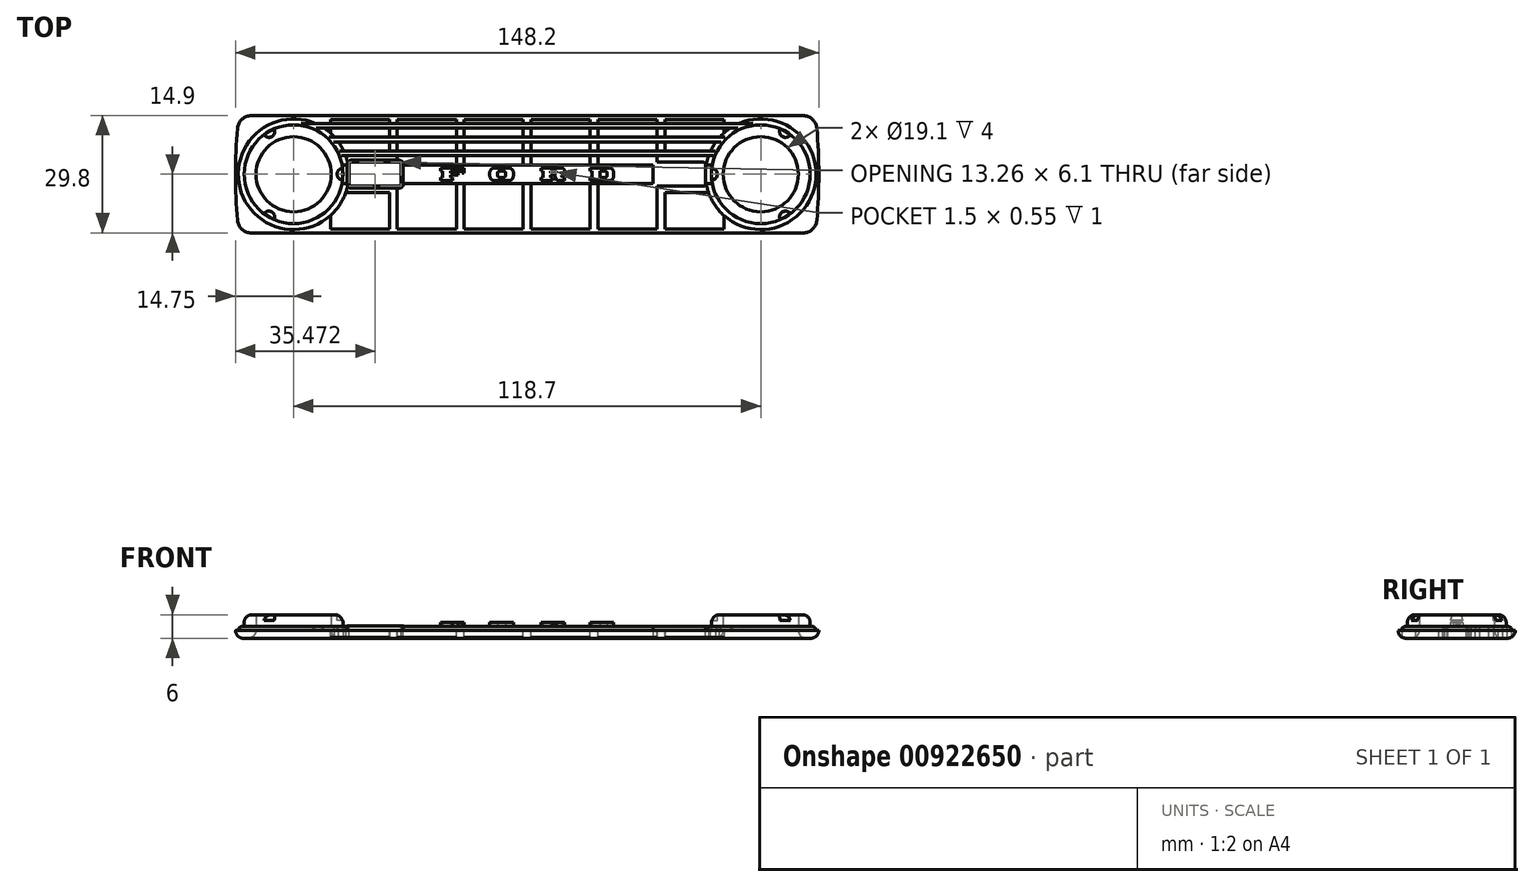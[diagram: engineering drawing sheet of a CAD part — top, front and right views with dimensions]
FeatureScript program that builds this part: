
annotation { "Feature Type Name" : "Feature", "Feature Type Description" : "" }
export const myFeature = defineFeature(function(context is Context, id is Id, definition is map)
    precondition{}
    {
        {
            var Q0;
            Q0=qCreatedBy(makeId("Top.planeOp"),FACE);
            var sketch = newSketch(context, id + "F0", { "sketchPlane" : qUnion([Q0])});
            skLineSegment(sketch, "E0.bottom", {"start": v(73.25, 14.9) * mm, "end": v(-73.25, 14.9) * mm});
            skLineSegment(sketch, "E0.top", {"start": v(73.25, -14.9) * mm, "end": v(-73.25, -14.9) * mm});
            skLineSegment(sketch, "E0.left", {"start": v(73.25, 14.9) * mm, "end": v(73.25, -14.9) * mm, "construction": true});
            skLineSegment(sketch, "E0.right", {"start": v(-73.25, 14.9) * mm, "end": v(-73.25, -14.9) * mm, "construction": true});
            skPoint(sketch, "E0.middle", {"position": v(0, 0) * mm});
            skLineSegment(sketch, "E1.0", {"start": v(-74.1, 15.75) * mm, "end": v(-74.1, -15.75) * mm, "construction": true});
            skLineSegment(sketch, "E1.2", {"start": v(74.1, 15.75) * mm, "end": v(74.1, -15.75) * mm, "construction": true});
            skPoint(sketch, "E2", {"position": v(-74.1, 0) * mm});
            skArc(sketch, "E3", {"start": v(-73.25, 14.9) * mm, "mid": v(-74.1, 0) * mm, "end": v(-73.25, -14.9) * mm});
            skArc(sketch, "E4.MirrorCS", {"start": v(73.25, 14.9) * mm, "mid": v(74.1, 0) * mm, "end": v(73.25, -14.9) * mm});
            skCircle(sketch, "E5", {"center": v(-59.35, 0) * mm, "radius": 9.55 * mm});
            skCircle(sketch, "E6.MirrorC", {"center": v(59.35, 0) * mm, "radius": 9.55 * mm});
            skSolve(sketch);
        }
        {
            var Q0;
            Q0 = qSketchRegion(id + "F0", true);
            extrude(context, id + "F1", {"entities" : qUnion([Q0]), "depth" : 2 * mm, "offsetDistance" : 25 * mm});
        }
        {
            var Q0;
            Q0=makeQuery(id+"F1.opExtrude","CAP_FACE",FACE,{"disambiguationData":[OSD([sQuery(id+"F0.wireOp",EDGE,"E0.bottom"),sQuery(id+"F0.wireOp",EDGE,"E0.top"),sQuery(id+"F0.wireOp",EDGE,"E3"),sQuery(id+"F0.wireOp",EDGE,"E4.MirrorCS"),sQuery(id+"F0.wireOp",EDGE,"E5"),sQuery(id+"F0.wireOp",EDGE,"E6.MirrorC")])],"isStart":true});
            var sketch = newSketch(context, id + "F2", { "sketchPlane" : qUnion([Q0])});
            skLineSegment(sketch, "E7", {"start": v(0, 14.9) * mm, "end": v(0, -14.9) * mm, "construction": true});
            skLineSegment(sketch, "E8.0", {"start": v(-1, 13.9) * mm, "end": v(-1, -13.9) * mm});
            skLineSegment(sketch, "E9.0", {"start": v(-16, 13.9) * mm, "end": v(-16, -13.9) * mm});
            skLineSegment(sketch, "E10.0", {"start": v(-18, 13.9) * mm, "end": v(-18, -13.9) * mm});
            skLineSegment(sketch, "E11.0", {"start": v(-33, 13.9) * mm, "end": v(-33, -13.9) * mm});
            skLineSegment(sketch, "E12.0", {"start": v(-35, 13.9) * mm, "end": v(-35, -13.9) * mm});
            skLineSegment(sketch, "E13.0", {"start": v(-50, 13.9) * mm, "end": v(-50, 10.49) * mm});
            skLineSegment(sketch, "E14.trimOffspring", {"start": v(-50, -10.49) * mm, "end": v(-50, -13.9) * mm});
            skArc(sketch, "E15.trimOffspring", {"start": v(-50, -10.49) * mm, "mid": v(-45.3, 0) * mm, "end": v(-50, 10.49) * mm});
            skLineSegment(sketch, "E16.trimOffspring", {"start": v(-35, -13.9) * mm, "end": v(-50, -13.9) * mm});
            skLineSegment(sketch, "E17.trimOffspring", {"start": v(-35, 13.9) * mm, "end": v(-50, 13.9) * mm});
            skLineSegment(sketch, "E18.trimOffspring", {"start": v(-18, 13.9) * mm, "end": v(-33, 13.9) * mm});
            skLineSegment(sketch, "E19.trimOffspring", {"start": v(-18, -13.9) * mm, "end": v(-33, -13.9) * mm});
            skLineSegment(sketch, "E20.trimOffspring", {"start": v(-1, -13.9) * mm, "end": v(-16, -13.9) * mm});
            skLineSegment(sketch, "E21.trimOffspring", {"start": v(-1, 13.9) * mm, "end": v(-16, 13.9) * mm});
            skLineSegment(sketch, "E22.MirrorCS", {"start": v(18, -13.9) * mm, "end": v(33, -13.9) * mm});
            skLineSegment(sketch, "E23.MirrorCS", {"start": v(18, 13.9) * mm, "end": v(18, -13.9) * mm});
            skLineSegment(sketch, "E24.MirrorCS", {"start": v(35, 13.9) * mm, "end": v(50, 13.9) * mm});
            skLineSegment(sketch, "E25.MirrorCS", {"start": v(18, 13.9) * mm, "end": v(33, 13.9) * mm});
            skLineSegment(sketch, "E26.MirrorCS", {"start": v(35, 13.9) * mm, "end": v(35, -13.9) * mm});
            skArc(sketch, "E27.MirrorCS", {"start": v(50, -10.49) * mm, "mid": v(45.3, 0) * mm, "end": v(50, 10.49) * mm});
            skLineSegment(sketch, "E28.MirrorCS", {"start": v(1, 13.9) * mm, "end": v(1, -13.9) * mm});
            skLineSegment(sketch, "E29.MirrorCS", {"start": v(16, 13.9) * mm, "end": v(16, -13.9) * mm});
            skLineSegment(sketch, "E30.MirrorCS", {"start": v(35, -13.9) * mm, "end": v(50, -13.9) * mm});
            skLineSegment(sketch, "E31.MirrorCS", {"start": v(33, 13.9) * mm, "end": v(33, -13.9) * mm});
            skLineSegment(sketch, "E32.MirrorCS", {"start": v(1, -13.9) * mm, "end": v(16, -13.9) * mm});
            skLineSegment(sketch, "E33.MirrorCS", {"start": v(1, 13.9) * mm, "end": v(16, 13.9) * mm});
            skLineSegment(sketch, "E34.MirrorCS", {"start": v(50, -10.49) * mm, "end": v(50, -13.9) * mm});
            skLineSegment(sketch, "E35.MirrorCS", {"start": v(50, 13.9) * mm, "end": v(50, 10.49) * mm});
            skSolve(sketch);
        }
        {
            var Q0;
            Q0 = qSketchRegion(id + "F2", true);
            extrude(context, id + "F3", {"entities" : qUnion([Q0]), "operationType" : NewBodyOperationType.REMOVE, "oppositeDirection" : true, "depth" : 25 * mm, "offsetDistance" : 25 * mm});
        }
        {
            var Q0;
            Q0=makeQuery(id+"F1.opExtrude","CAP_FACE",FACE,{"disambiguationData":[OSD([sQuery(id+"F0.wireOp",EDGE,"E0.bottom"),sQuery(id+"F0.wireOp",EDGE,"E0.top"),sQuery(id+"F0.wireOp",EDGE,"E3"),sQuery(id+"F0.wireOp",EDGE,"E4.MirrorCS"),sQuery(id+"F0.wireOp",EDGE,"E5"),sQuery(id+"F0.wireOp",EDGE,"E6.MirrorC")])],"isStart":false});
            var sketch = newSketch(context, id + "F4", { "sketchPlane" : qUnion([Q0])});
            skCircle(sketch, "E36.0", {"center": v(59.35, 0) * mm, "radius": 9.55 * mm});
            skCircle(sketch, "E36.1", {"center": v(-59.35, 0) * mm, "radius": 9.55 * mm});
            skCircle(sketch, "E37.0", {"center": v(-59.35, 0) * mm, "radius": 14.05 * mm});
            skCircle(sketch, "E38.0", {"center": v(59.35, 0) * mm, "radius": 14.05 * mm});
            skSolve(sketch);
        }
        {
            var Q0;
            Q0 = qSketchRegion(id + "F4", true);
            extrude(context, id + "F5", {"entities" : qUnion([Q0]), "operationType" : NewBodyOperationType.ADD, "depth" : 1 * mm, "offsetDistance" : 25 * mm});
        }
        {
            var Q0;
            Q0=makeQuery(id+"F5.opExtrude","CAP_FACE",FACE,{"disambiguationData":[OSD([sQuery(id+"F4.wireOp",EDGE,"E36.1"),sQuery(id+"F4.wireOp",EDGE,"E37.0")])],"isStart":false});
            var sketch = newSketch(context, id + "F6", { "sketchPlane" : qUnion([Q0])});
            skLineSegment(sketch, "E39.0", {"start": v(-50, 13.9) * mm, "end": v(-35, 13.9) * mm, "construction": true});
            skLineSegment(sketch, "E40.0", {"start": v(-53.78, 12.9) * mm, "end": v(53.78, 12.9) * mm});
            skArc(sketch, "E41.0", {"start": v(-46.1, 4.7) * mm, "mid": v(-46.34, 5.3) * mm, "end": v(-46.6, 5.9) * mm});
            skArc(sketch, "E42.0", {"start": v(53.78, 12.9) * mm, "mid": v(52.65, 12.35) * mm, "end": v(51.57, 11.7) * mm});
            skLineSegment(sketch, "E43.0", {"start": v(-51.57, 11.7) * mm, "end": v(51.57, 11.7) * mm});
            skLineSegment(sketch, "E44.0", {"start": v(-48.9, 9.4) * mm, "end": v(48.9, 9.4) * mm});
            skLineSegment(sketch, "E45.0", {"start": v(-47.94, 8.2) * mm, "end": v(47.94, 8.2) * mm});
            skLineSegment(sketch, "E46.0", {"start": v(-46.6, 5.9) * mm, "end": v(46.6, 5.9) * mm});
            skLineSegment(sketch, "E47.0", {"start": v(-46.1, 4.7) * mm, "end": v(46.1, 4.7) * mm});
            skLineSegment(sketch, "E48.0", {"start": v(-45.5, 2.4) * mm, "end": v(45.5, 2.4) * mm});
            skLineSegment(sketch, "E49", {"start": v(-45.3, 0) * mm, "end": v(45.3, 0) * mm});
            skArc(sketch, "E50.trimOffspring", {"start": v(45.5, 2.4) * mm, "mid": v(45.35, 1.2) * mm, "end": v(45.3, 0) * mm});
            skArc(sketch, "E51.trimOffspring", {"start": v(46.6, 5.9) * mm, "mid": v(46.34, 5.3) * mm, "end": v(46.1, 4.7) * mm});
            skArc(sketch, "E52.trimOffspring", {"start": v(48.9, 9.4) * mm, "mid": v(48.4, 8.81) * mm, "end": v(47.94, 8.2) * mm});
            skArc(sketch, "E53.trimOffspring", {"start": v(-47.94, 8.2) * mm, "mid": v(-48.4, 8.81) * mm, "end": v(-48.9, 9.4) * mm});
            skArc(sketch, "E54.trimOffspring", {"start": v(-51.57, 11.7) * mm, "mid": v(-71.12, -7.67) * mm, "end": v(-45.5, 2.4) * mm});
            skArc(sketch, "E55.MirrorCS", {"start": v(-46.1, -4.7) * mm, "mid": v(-46.34, -5.3) * mm, "end": v(-46.6, -5.9) * mm});
            skArc(sketch, "E56.MirrorCS", {"start": v(45.5, -2.4) * mm, "mid": v(45.35, -1.2) * mm, "end": v(45.3, 0) * mm});
            skArc(sketch, "E57.MirrorCS", {"start": v(-47.94, -8.2) * mm, "mid": v(-48.4, -8.81) * mm, "end": v(-48.9, -9.4) * mm});
            skArc(sketch, "E58.MirrorCS", {"start": v(46.6, -5.9) * mm, "mid": v(46.34, -5.3) * mm, "end": v(46.1, -4.7) * mm});
            skArc(sketch, "E59.MirrorCS", {"start": v(53.78, -12.9) * mm, "mid": v(52.65, -12.35) * mm, "end": v(51.57, -11.7) * mm});
            skArc(sketch, "E60.MirrorCS", {"start": v(48.9, -9.4) * mm, "mid": v(48.4, -8.81) * mm, "end": v(47.94, -8.2) * mm});
            skLineSegment(sketch, "E61.MirrorCS", {"start": v(-53.78, -12.9) * mm, "end": v(53.78, -12.9) * mm});
            skLineSegment(sketch, "E62.MirrorCS", {"start": v(-46.1, -4.7) * mm, "end": v(46.1, -4.7) * mm});
            skLineSegment(sketch, "E63.MirrorCS", {"start": v(-48.9, -9.4) * mm, "end": v(48.9, -9.4) * mm});
            skLineSegment(sketch, "E64.MirrorCS", {"start": v(-46.6, -5.9) * mm, "end": v(46.6, -5.9) * mm});
            skLineSegment(sketch, "E65.MirrorCS", {"start": v(-51.57, -11.7) * mm, "end": v(51.57, -11.7) * mm});
            skLineSegment(sketch, "E66.MirrorCS", {"start": v(-47.94, -8.2) * mm, "end": v(47.94, -8.2) * mm});
            skLineSegment(sketch, "E67.MirrorCS", {"start": v(-45.5, -2.4) * mm, "end": v(45.5, -2.4) * mm});
            skLineSegment(sketch, "E68.MirrorCS", {"start": v(-50, -13.9) * mm, "end": v(-35, -13.9) * mm, "construction": true});
            skSolve(sketch);
        }
        {
            var Q0;
            {var subQ0=sQuery(id+"F6.wireOp",EDGE,"E49");var subQ1=makeQuery(id+"F6.imprint","IMPRINT",EDGE,{"derivedFrom":subQ0});var subQ7=sQuery(id+"F6.wireOp",EDGE,"E48.0");var subQ11=sQuery(id+"F6.wireOp",EDGE,"E40.0");Q0=qUnion([makeQuery(id+"F6.imprint","IMPRINT",FACE,{"disambiguationData":[TD([[makeQuery(id+"F6.imprint","IMPRINT",EDGE,{"derivedFrom":sQuery(id+"F6.wireOp",EDGE,"E44.0")}),-1.0]])]}),makeQuery(id+"F6.imprint","IMPRINT",FACE,{"disambiguationData":[TD([[makeQuery(id+"F6.imprint","IMPRINT",EDGE,{"derivedFrom":sQuery(id+"F6.wireOp",EDGE,"E59.MirrorCS")}),1.0]])]}),makeQuery(id+"F6.imprint","IMPRINT",FACE,{"disambiguationData":[TD([[makeQuery(id+"F6.imprint","IMPRINT",EDGE,{"derivedFrom":subQ11}),-1.0]])]}),makeQuery(id+"F6.imprint","IMPRINT",FACE,{"disambiguationData":[TD([[makeQuery(id+"F6.imprint","IMPRINT",EDGE,{"derivedFrom":sQuery(id+"F6.wireOp",EDGE,"E60.MirrorCS")}),1.0]])]}),makeQuery(id+"F6.imprint","IMPRINT",FACE,{"disambiguationData":[TD([[makeQuery(id+"F6.imprint","IMPRINT",EDGE,{"derivedFrom":subQ7}),-1.0]])]}),makeQuery(id+"F6.imprint","IMPRINT",FACE,{"disambiguationData":[TD([[makeQuery(id+"F6.imprint","IMPRINT",EDGE,{"derivedFrom":sQuery(id+"F6.wireOp",EDGE,"E41.0")}),-1.0]])]}),makeQuery(id+"F6.imprint","IMPRINT",FACE,{"disambiguationData":[TD([[makeQuery(id+"F6.imprint","IMPRINT",EDGE,{"derivedFrom":sQuery(id+"F6.wireOp",EDGE,"E58.MirrorCS")}),1.0]])]}),makeQuery(id+"F6.imprint","IMPRINT",FACE,{"disambiguationData":[TD([[subQ1,-1.0]])]})]);}
            extrude(context, id + "F7", {"entities" : qUnion([Q0]), "operationType" : NewBodyOperationType.ADD, "oppositeDirection" : true, "depth" : 3 * mm, "offsetDistance" : 25 * mm});
        }
        {
            var Q0;
            {var subQ0=sQuery(id+"F6.wireOp",EDGE,"E54.trimOffspring");Q0=makeQuery(id+"F7.boolean.opBoolean","MERGE",FACE,{"derivedFrom":[makeQuery(id+"F5.opExtrude","CAP_FACE",FACE,{"disambiguationData":[OSD([sQuery(id+"F4.wireOp",EDGE,"E36.0"),sQuery(id+"F4.wireOp",EDGE,"E38.0")])],"isStart":false}),makeQuery(id+"F5.opExtrude","CAP_FACE",FACE,{"disambiguationData":[OSD([sQuery(id+"F4.wireOp",EDGE,"E36.1"),sQuery(id+"F4.wireOp",EDGE,"E37.0")])],"isStart":false}),makeQuery(id+"F7.opExtrude","CAP_FACE",FACE,{"disambiguationData":[OSD([sQuery(id+"F6.wireOp",EDGE,"E40.0"),sQuery(id+"F6.wireOp",EDGE,"E42.0"),sQuery(id+"F6.wireOp",EDGE,"E43.0"),subQ0])],"isStart":true}),makeQuery(id+"F7.opExtrude","CAP_FACE",FACE,{"disambiguationData":[OSD([sQuery(id+"F6.wireOp",EDGE,"E41.0"),sQuery(id+"F6.wireOp",EDGE,"E46.0"),sQuery(id+"F6.wireOp",EDGE,"E47.0"),sQuery(id+"F6.wireOp",EDGE,"E51.trimOffspring")])],"isStart":true}),makeQuery(id+"F7.opExtrude","CAP_FACE",FACE,{"disambiguationData":[OSD([sQuery(id+"F6.wireOp",EDGE,"E44.0"),sQuery(id+"F6.wireOp",EDGE,"E45.0"),sQuery(id+"F6.wireOp",EDGE,"E52.trimOffspring"),sQuery(id+"F6.wireOp",EDGE,"E53.trimOffspring")])],"isStart":true}),makeQuery(id+"F7.opExtrude","CAP_FACE",FACE,{"disambiguationData":[OSD([sQuery(id+"F6.wireOp",EDGE,"E48.0"),sQuery(id+"F6.wireOp",EDGE,"E50.trimOffspring"),subQ0,sQuery(id+"F6.wireOp",EDGE,"E56.MirrorCS"),sQuery(id+"F6.wireOp",EDGE,"E67.MirrorCS")])],"isStart":true}),makeQuery(id+"F7.opExtrude","CAP_FACE",FACE,{"disambiguationData":[OSD([subQ0,sQuery(id+"F6.wireOp",EDGE,"E59.MirrorCS"),sQuery(id+"F6.wireOp",EDGE,"E61.MirrorCS"),sQuery(id+"F6.wireOp",EDGE,"E65.MirrorCS")])],"isStart":true}),makeQuery(id+"F7.opExtrude","CAP_FACE",FACE,{"disambiguationData":[OSD([subQ0,sQuery(id+"F6.wireOp",EDGE,"E60.MirrorCS"),sQuery(id+"F6.wireOp",EDGE,"E63.MirrorCS"),sQuery(id+"F6.wireOp",EDGE,"E66.MirrorCS")])],"isStart":true}),makeQuery(id+"F7.opExtrude","CAP_FACE",FACE,{"disambiguationData":[OSD([subQ0,sQuery(id+"F6.wireOp",EDGE,"E58.MirrorCS"),sQuery(id+"F6.wireOp",EDGE,"E62.MirrorCS"),sQuery(id+"F6.wireOp",EDGE,"E64.MirrorCS")])],"isStart":true})]});}
            var sketch = newSketch(context, id + "F8", { "sketchPlane" : qUnion([Q0])});
            skCircle(sketch, "E69.0", {"center": v(-59.35, 0) * mm, "radius": 9.55 * mm});
            skCircle(sketch, "E69.1", {"center": v(59.35, 0) * mm, "radius": 9.55 * mm});
            skCircle(sketch, "E70.0", {"center": v(-59.35, 0) * mm, "radius": 12.55 * mm});
            skCircle(sketch, "E71.0", {"center": v(59.35, 0) * mm, "radius": 12.55 * mm});
            skSolve(sketch);
        }
        {
            var Q0;
            Q0 = qSketchRegion(id + "F8", true);
            extrude(context, id + "F9", {"entities" : qUnion([Q0]), "operationType" : NewBodyOperationType.ADD, "depth" : 3 * mm, "offsetDistance" : 25 * mm});
        }
        {
            var Q0;
            Q0=makeQuery(id+"F9.opExtrude","CAP_EDGE",EDGE,{"disambiguationData":[OSD([sQuery(id+"F8.wireOp",EDGE,"E70.0")])],"isStart":false});
            var Q1;
            Q1=makeQuery(id+"F9.opExtrude","CAP_EDGE",EDGE,{"disambiguationData":[OSD([sQuery(id+"F8.wireOp",EDGE,"E71.0")])],"isStart":false});
            fillet(context, id + "F10", {"entities" : qUnion([Q0, Q1]), "radius" : 2 * mm, "tangentPropagation" : true, "allowEdgeOverflow" : false});
        }
        {
            var Q0;
            {var subQ2=sQuery(id+"F6.wireOp",EDGE,"E40.0");var subQ3=sQuery(id+"F4.wireOp",EDGE,"E37.0");Q0=makeQuery(id+"F7.boolean.opBoolean","SPLIT",EDGE,{"disambiguationData":[TD([makeQuery(id+"F7.opExtrude","SWEPT_FACE",FACE,{"disambiguationData":[OSD([subQ2])]})])],"derivedFrom":makeQuery(id+"F5.opExtrude","CAP_EDGE",EDGE,{"disambiguationData":[OSD([subQ3])],"isStart":false})});}
            var Q1;
            {var subQ1=sQuery(id+"F6.wireOp",EDGE,"E43.0");var subQ3=sQuery(id+"F4.wireOp",EDGE,"E37.0");Q1=makeQuery(id+"F7.boolean.opBoolean","SPLIT",EDGE,{"disambiguationData":[TD([makeQuery(id+"F7.opExtrude","SWEPT_FACE",FACE,{"disambiguationData":[OSD([subQ1])]})])],"derivedFrom":makeQuery(id+"F5.opExtrude","CAP_EDGE",EDGE,{"disambiguationData":[OSD([subQ3])],"isStart":false})});}
            var Q2;
            {var subQ0=sQuery(id+"F6.wireOp",EDGE,"E45.0");var subQ3=sQuery(id+"F4.wireOp",EDGE,"E37.0");Q2=makeQuery(id+"F7.boolean.opBoolean","SPLIT",EDGE,{"disambiguationData":[TD([makeQuery(id+"F7.opExtrude","SWEPT_FACE",FACE,{"disambiguationData":[OSD([subQ0])]})])],"derivedFrom":makeQuery(id+"F5.opExtrude","CAP_EDGE",EDGE,{"disambiguationData":[OSD([subQ3])],"isStart":false})});}
            var Q3;
            {var subQ0=sQuery(id+"F6.wireOp",EDGE,"E47.0");var subQ3=sQuery(id+"F4.wireOp",EDGE,"E37.0");Q3=makeQuery(id+"F7.boolean.opBoolean","SPLIT",EDGE,{"disambiguationData":[TD([makeQuery(id+"F7.opExtrude","SWEPT_FACE",FACE,{"disambiguationData":[OSD([subQ0])]})])],"derivedFrom":makeQuery(id+"F5.opExtrude","CAP_EDGE",EDGE,{"disambiguationData":[OSD([subQ3])],"isStart":false})});}
            var Q4;
            {var subQ1=sQuery(id+"F4.wireOp",EDGE,"E37.0");var subQ3=sQuery(id+"F6.wireOp",EDGE,"E62.MirrorCS");Q4=makeQuery(id+"F7.boolean.opBoolean","SPLIT",EDGE,{"disambiguationData":[TD([makeQuery(id+"F7.opExtrude","SWEPT_FACE",FACE,{"disambiguationData":[OSD([subQ3])]})])],"derivedFrom":makeQuery(id+"F5.opExtrude","CAP_EDGE",EDGE,{"disambiguationData":[OSD([subQ1])],"isStart":false})});}
            var Q5;
            {var subQ2=sQuery(id+"F4.wireOp",EDGE,"E37.0");var subQ3=sQuery(id+"F6.wireOp",EDGE,"E64.MirrorCS");Q5=makeQuery(id+"F7.boolean.opBoolean","SPLIT",EDGE,{"disambiguationData":[TD([makeQuery(id+"F7.opExtrude","SWEPT_FACE",FACE,{"disambiguationData":[OSD([subQ3])]})])],"derivedFrom":makeQuery(id+"F5.opExtrude","CAP_EDGE",EDGE,{"disambiguationData":[OSD([subQ2])],"isStart":false})});}
            var Q6;
            {var subQ0=sQuery(id+"F6.wireOp",EDGE,"E63.MirrorCS");var subQ3=sQuery(id+"F4.wireOp",EDGE,"E37.0");Q6=makeQuery(id+"F7.boolean.opBoolean","SPLIT",EDGE,{"disambiguationData":[TD([makeQuery(id+"F7.opExtrude","SWEPT_FACE",FACE,{"disambiguationData":[OSD([subQ0])]})])],"derivedFrom":makeQuery(id+"F5.opExtrude","CAP_EDGE",EDGE,{"disambiguationData":[OSD([subQ3])],"isStart":false})});}
            fillet(context, id + "F11", {"entities" : qUnion([Q0, Q1, Q2, Q3, Q4, Q5, Q6]), "radius" : 1 * mm, "tangentPropagation" : true, "allowEdgeOverflow" : false});
        }
        {
            var Q0;
            {var subQ2=sQuery(id+"F6.wireOp",EDGE,"E40.0");var subQ3=sQuery(id+"F4.wireOp",EDGE,"E38.0");Q0=makeQuery(id+"F7.boolean.opBoolean","SPLIT",EDGE,{"disambiguationData":[TD([makeQuery(id+"F7.opExtrude","SWEPT_FACE",FACE,{"disambiguationData":[OSD([subQ2])]})])],"derivedFrom":makeQuery(id+"F5.opExtrude","CAP_EDGE",EDGE,{"disambiguationData":[OSD([subQ3])],"isStart":false})});}
            var Q1;
            {var subQ1=sQuery(id+"F6.wireOp",EDGE,"E43.0");var subQ3=sQuery(id+"F4.wireOp",EDGE,"E38.0");Q1=makeQuery(id+"F7.boolean.opBoolean","SPLIT",EDGE,{"disambiguationData":[TD([makeQuery(id+"F7.opExtrude","SWEPT_FACE",FACE,{"disambiguationData":[OSD([subQ1])]})])],"derivedFrom":makeQuery(id+"F5.opExtrude","CAP_EDGE",EDGE,{"disambiguationData":[OSD([subQ3])],"isStart":false})});}
            var Q2;
            {var subQ0=sQuery(id+"F6.wireOp",EDGE,"E45.0");var subQ3=sQuery(id+"F4.wireOp",EDGE,"E38.0");Q2=makeQuery(id+"F7.boolean.opBoolean","SPLIT",EDGE,{"disambiguationData":[TD([makeQuery(id+"F7.opExtrude","SWEPT_FACE",FACE,{"disambiguationData":[OSD([subQ0])]})])],"derivedFrom":makeQuery(id+"F5.opExtrude","CAP_EDGE",EDGE,{"disambiguationData":[OSD([subQ3])],"isStart":false})});}
            var Q3;
            {var subQ0=sQuery(id+"F6.wireOp",EDGE,"E47.0");var subQ3=sQuery(id+"F4.wireOp",EDGE,"E38.0");Q3=makeQuery(id+"F7.boolean.opBoolean","SPLIT",EDGE,{"disambiguationData":[TD([makeQuery(id+"F7.opExtrude","SWEPT_FACE",FACE,{"disambiguationData":[OSD([subQ0])]})])],"derivedFrom":makeQuery(id+"F5.opExtrude","CAP_EDGE",EDGE,{"disambiguationData":[OSD([subQ3])],"isStart":false})});}
            var Q4;
            {var subQ2=sQuery(id+"F4.wireOp",EDGE,"E38.0");var subQ3=sQuery(id+"F6.wireOp",EDGE,"E62.MirrorCS");Q4=makeQuery(id+"F7.boolean.opBoolean","SPLIT",EDGE,{"disambiguationData":[TD([makeQuery(id+"F7.opExtrude","SWEPT_FACE",FACE,{"disambiguationData":[OSD([subQ3])]})])],"derivedFrom":makeQuery(id+"F5.opExtrude","CAP_EDGE",EDGE,{"disambiguationData":[OSD([subQ2])],"isStart":false})});}
            var Q5;
            {var subQ1=sQuery(id+"F6.wireOp",EDGE,"E64.MirrorCS");var subQ3=sQuery(id+"F4.wireOp",EDGE,"E38.0");Q5=makeQuery(id+"F7.boolean.opBoolean","SPLIT",EDGE,{"disambiguationData":[TD([makeQuery(id+"F7.opExtrude","SWEPT_FACE",FACE,{"disambiguationData":[OSD([subQ1])]})])],"derivedFrom":makeQuery(id+"F5.opExtrude","CAP_EDGE",EDGE,{"disambiguationData":[OSD([subQ3])],"isStart":false})});}
            var Q6;
            {var subQ2=sQuery(id+"F6.wireOp",EDGE,"E63.MirrorCS");var subQ3=sQuery(id+"F4.wireOp",EDGE,"E38.0");Q6=makeQuery(id+"F7.boolean.opBoolean","SPLIT",EDGE,{"disambiguationData":[TD([makeQuery(id+"F7.opExtrude","SWEPT_FACE",FACE,{"disambiguationData":[OSD([subQ2])]})])],"derivedFrom":makeQuery(id+"F5.opExtrude","CAP_EDGE",EDGE,{"disambiguationData":[OSD([subQ3])],"isStart":false})});}
            fillet(context, id + "F12", {"entities" : qUnion([Q0, Q1, Q2, Q3, Q4, Q5, Q6]), "radius" : 1 * mm, "tangentPropagation" : true, "allowEdgeOverflow" : false});
        }
        {
            var Q0;
            Q0=makeQuery(id+"F1.opExtrude","SWEPT_EDGE",EDGE,{"disambiguationData":[OSD([sQuery(id+"F0.wireOp",EDGE,"E0.bottom"),sQuery(id+"F0.wireOp",EDGE,"E4.MirrorCS")])]});
            var Q1;
            Q1=makeQuery(id+"F1.opExtrude","SWEPT_EDGE",EDGE,{"disambiguationData":[OSD([sQuery(id+"F0.wireOp",EDGE,"E0.top"),sQuery(id+"F0.wireOp",EDGE,"E4.MirrorCS")])]});
            var Q2;
            Q2=makeQuery(id+"F1.opExtrude","SWEPT_EDGE",EDGE,{"disambiguationData":[OSD([sQuery(id+"F0.wireOp",EDGE,"E0.bottom"),sQuery(id+"F0.wireOp",EDGE,"E3")])]});
            var Q3;
            Q3=makeQuery(id+"F1.opExtrude","SWEPT_EDGE",EDGE,{"disambiguationData":[OSD([sQuery(id+"F0.wireOp",EDGE,"E0.top"),sQuery(id+"F0.wireOp",EDGE,"E3")])]});
            fillet(context, id + "F13", {"entities" : qUnion([Q0, Q1, Q2, Q3]), "radius" : 3.5 * mm, "tangentPropagation" : true, "allowEdgeOverflow" : false});
        }
        {
            var Q0;
            Q0=makeQuery(id+"F1.opExtrude","CAP_EDGE",EDGE,{"disambiguationData":[OSD([sQuery(id+"F0.wireOp",EDGE,"E0.bottom")])],"isStart":true});
            var Q1;
            Q1=makeQuery(id+"F1.opExtrude","CAP_EDGE",EDGE,{"disambiguationData":[OSD([sQuery(id+"F0.wireOp",EDGE,"E6.MirrorC")])],"isStart":true});
            var Q2;
            Q2=makeQuery(id+"F1.opExtrude","CAP_EDGE",EDGE,{"disambiguationData":[OSD([sQuery(id+"F0.wireOp",EDGE,"E5")])],"isStart":true});
            fillet(context, id + "F14", {"entities" : qUnion([Q0, Q1, Q2]), "radius" : 2 * mm, "tangentPropagation" : true, "allowEdgeOverflow" : false});
        }
        {
            var Q0;
            {var subQ0=sQuery(id+"F6.wireOp",EDGE,"E54.trimOffspring");Q0=makeQuery(id+"F7.boolean.opBoolean","MERGE",FACE,{"derivedFrom":[makeQuery(id+"F1.opExtrude","CAP_FACE",FACE,{"disambiguationData":[OSD([sQuery(id+"F0.wireOp",EDGE,"E0.bottom"),sQuery(id+"F0.wireOp",EDGE,"E0.top"),sQuery(id+"F0.wireOp",EDGE,"E3"),sQuery(id+"F0.wireOp",EDGE,"E4.MirrorCS"),sQuery(id+"F0.wireOp",EDGE,"E5"),sQuery(id+"F0.wireOp",EDGE,"E6.MirrorC")])],"isStart":true}),makeQuery(id+"F7.opExtrude","CAP_FACE",FACE,{"disambiguationData":[OSD([sQuery(id+"F6.wireOp",EDGE,"E40.0"),sQuery(id+"F6.wireOp",EDGE,"E42.0"),sQuery(id+"F6.wireOp",EDGE,"E43.0"),subQ0])],"isStart":false}),makeQuery(id+"F7.opExtrude","CAP_FACE",FACE,{"disambiguationData":[OSD([sQuery(id+"F6.wireOp",EDGE,"E41.0"),sQuery(id+"F6.wireOp",EDGE,"E46.0"),sQuery(id+"F6.wireOp",EDGE,"E47.0"),sQuery(id+"F6.wireOp",EDGE,"E51.trimOffspring")])],"isStart":false}),makeQuery(id+"F7.opExtrude","CAP_FACE",FACE,{"disambiguationData":[OSD([sQuery(id+"F6.wireOp",EDGE,"E44.0"),sQuery(id+"F6.wireOp",EDGE,"E45.0"),sQuery(id+"F6.wireOp",EDGE,"E52.trimOffspring"),sQuery(id+"F6.wireOp",EDGE,"E53.trimOffspring")])],"isStart":false}),makeQuery(id+"F7.opExtrude","CAP_FACE",FACE,{"disambiguationData":[OSD([sQuery(id+"F6.wireOp",EDGE,"E48.0"),sQuery(id+"F6.wireOp",EDGE,"E50.trimOffspring"),subQ0,sQuery(id+"F6.wireOp",EDGE,"E56.MirrorCS"),sQuery(id+"F6.wireOp",EDGE,"E67.MirrorCS")])],"isStart":false}),makeQuery(id+"F7.opExtrude","CAP_FACE",FACE,{"disambiguationData":[OSD([subQ0,sQuery(id+"F6.wireOp",EDGE,"E59.MirrorCS"),sQuery(id+"F6.wireOp",EDGE,"E61.MirrorCS"),sQuery(id+"F6.wireOp",EDGE,"E65.MirrorCS")])],"isStart":false}),makeQuery(id+"F7.opExtrude","CAP_FACE",FACE,{"disambiguationData":[OSD([subQ0,sQuery(id+"F6.wireOp",EDGE,"E60.MirrorCS"),sQuery(id+"F6.wireOp",EDGE,"E63.MirrorCS"),sQuery(id+"F6.wireOp",EDGE,"E66.MirrorCS")])],"isStart":false}),makeQuery(id+"F7.opExtrude","CAP_FACE",FACE,{"disambiguationData":[OSD([subQ0,sQuery(id+"F6.wireOp",EDGE,"E58.MirrorCS"),sQuery(id+"F6.wireOp",EDGE,"E62.MirrorCS"),sQuery(id+"F6.wireOp",EDGE,"E64.MirrorCS")])],"isStart":false})]});}
            var sketch = newSketch(context, id + "F15", { "sketchPlane" : qUnion([Q0])});
            skLineSegment(sketch, "E72.0", {"start": v(35, -2.4) * mm, "end": v(45.5, -2.4) * mm});
            skArc(sketch, "E72.1", {"start": v(45.5, 2.4) * mm, "mid": v(45.76, 3.56) * mm, "end": v(46.1, 4.7) * mm});
            skLineSegment(sketch, "E72.2", {"start": v(35, 4.7) * mm, "end": v(46.1, 4.7) * mm});
            skLineSegment(sketch, "E72.3", {"start": v(35, 2.4) * mm, "end": v(45.5, 2.4) * mm});
            skLineSegment(sketch, "E72.4", {"start": v(35, 4.7) * mm, "end": v(35, 2.4) * mm});
            skLineSegment(sketch, "E72.5", {"start": v(35, -2.4) * mm, "end": v(35, -4.7) * mm});
            skArc(sketch, "E72.6", {"start": v(46.1, -4.7) * mm, "mid": v(45.76, -3.56) * mm, "end": v(45.5, -2.4) * mm});
            skLineSegment(sketch, "E72.7", {"start": v(35, -4.7) * mm, "end": v(46.1, -4.7) * mm});
            skLineSegment(sketch, "E72.8", {"start": v(-45.5, 2.4) * mm, "end": v(-35, 2.4) * mm});
            skLineSegment(sketch, "E72.9", {"start": v(-45.5, -2.4) * mm, "end": v(-35, -2.4) * mm});
            skLineSegment(sketch, "E72.10", {"start": v(-46.1, -4.7) * mm, "end": v(-35, -4.7) * mm});
            skLineSegment(sketch, "E72.11", {"start": v(-35, -2.4) * mm, "end": v(-35, -4.7) * mm});
            skArc(sketch, "E72.12", {"start": v(-46.1, -4.7) * mm, "mid": v(-45.76, -3.56) * mm, "end": v(-45.5, -2.4) * mm});
            skArc(sketch, "E72.13", {"start": v(-45.5, 2.4) * mm, "mid": v(-45.76, 3.56) * mm, "end": v(-46.1, 4.7) * mm});
            skLineSegment(sketch, "E72.14", {"start": v(-35, 4.7) * mm, "end": v(-35, 2.4) * mm});
            skLineSegment(sketch, "E72.15", {"start": v(-46.1, 4.7) * mm, "end": v(-35, 4.7) * mm});
            skSolve(sketch);
        }
        {
            var Q0;
            Q0 = qSketchRegion(id + "F15", true);
            extrude(context, id + "F16", {"entities" : qUnion([Q0]), "operationType" : NewBodyOperationType.ADD, "oppositeDirection" : true, "depth" : 2 * mm, "offsetDistance" : 25 * mm});
        }
        {
            var Q0;
            {var subQ0=sQuery(id+"F6.wireOp",EDGE,"E54.trimOffspring");Q0=makeQuery(id+"F16.boolean.opBoolean","MERGE",FACE,{"derivedFrom":[makeQuery(id+"F7.boolean.opBoolean","MERGE",FACE,{"derivedFrom":[makeQuery(id+"F1.opExtrude","CAP_FACE",FACE,{"disambiguationData":[OSD([sQuery(id+"F0.wireOp",EDGE,"E0.bottom"),sQuery(id+"F0.wireOp",EDGE,"E0.top"),sQuery(id+"F0.wireOp",EDGE,"E3"),sQuery(id+"F0.wireOp",EDGE,"E4.MirrorCS"),sQuery(id+"F0.wireOp",EDGE,"E5"),sQuery(id+"F0.wireOp",EDGE,"E6.MirrorC")])],"isStart":true}),makeQuery(id+"F7.opExtrude","CAP_FACE",FACE,{"disambiguationData":[OSD([sQuery(id+"F6.wireOp",EDGE,"E40.0"),sQuery(id+"F6.wireOp",EDGE,"E42.0"),sQuery(id+"F6.wireOp",EDGE,"E43.0"),subQ0])],"isStart":false}),makeQuery(id+"F7.opExtrude","CAP_FACE",FACE,{"disambiguationData":[OSD([sQuery(id+"F6.wireOp",EDGE,"E41.0"),sQuery(id+"F6.wireOp",EDGE,"E46.0"),sQuery(id+"F6.wireOp",EDGE,"E47.0"),sQuery(id+"F6.wireOp",EDGE,"E51.trimOffspring")])],"isStart":false}),makeQuery(id+"F7.opExtrude","CAP_FACE",FACE,{"disambiguationData":[OSD([sQuery(id+"F6.wireOp",EDGE,"E44.0"),sQuery(id+"F6.wireOp",EDGE,"E45.0"),sQuery(id+"F6.wireOp",EDGE,"E52.trimOffspring"),sQuery(id+"F6.wireOp",EDGE,"E53.trimOffspring")])],"isStart":false}),makeQuery(id+"F7.opExtrude","CAP_FACE",FACE,{"disambiguationData":[OSD([sQuery(id+"F6.wireOp",EDGE,"E48.0"),sQuery(id+"F6.wireOp",EDGE,"E50.trimOffspring"),subQ0,sQuery(id+"F6.wireOp",EDGE,"E56.MirrorCS"),sQuery(id+"F6.wireOp",EDGE,"E67.MirrorCS")])],"isStart":false}),makeQuery(id+"F7.opExtrude","CAP_FACE",FACE,{"disambiguationData":[OSD([subQ0,sQuery(id+"F6.wireOp",EDGE,"E59.MirrorCS"),sQuery(id+"F6.wireOp",EDGE,"E61.MirrorCS"),sQuery(id+"F6.wireOp",EDGE,"E65.MirrorCS")])],"isStart":false}),makeQuery(id+"F7.opExtrude","CAP_FACE",FACE,{"disambiguationData":[OSD([subQ0,sQuery(id+"F6.wireOp",EDGE,"E60.MirrorCS"),sQuery(id+"F6.wireOp",EDGE,"E63.MirrorCS"),sQuery(id+"F6.wireOp",EDGE,"E66.MirrorCS")])],"isStart":false}),makeQuery(id+"F7.opExtrude","CAP_FACE",FACE,{"disambiguationData":[OSD([subQ0,sQuery(id+"F6.wireOp",EDGE,"E58.MirrorCS"),sQuery(id+"F6.wireOp",EDGE,"E62.MirrorCS"),sQuery(id+"F6.wireOp",EDGE,"E64.MirrorCS")])],"isStart":false})]}),makeQuery(id+"F16.opExtrude","CAP_FACE",FACE,{"disambiguationData":[OSD([sQuery(id+"F15.wireOp",EDGE,"E72.0"),sQuery(id+"F15.wireOp",EDGE,"E72.5"),sQuery(id+"F15.wireOp",EDGE,"E72.6"),sQuery(id+"F15.wireOp",EDGE,"E72.7")])],"isStart":true}),makeQuery(id+"F16.opExtrude","CAP_FACE",FACE,{"disambiguationData":[OSD([sQuery(id+"F15.wireOp",EDGE,"E72.1"),sQuery(id+"F15.wireOp",EDGE,"E72.2"),sQuery(id+"F15.wireOp",EDGE,"E72.3"),sQuery(id+"F15.wireOp",EDGE,"E72.4")])],"isStart":true}),makeQuery(id+"F16.opExtrude","CAP_FACE",FACE,{"disambiguationData":[OSD([sQuery(id+"F15.wireOp",EDGE,"E72.8"),sQuery(id+"F15.wireOp",EDGE,"E72.13"),sQuery(id+"F15.wireOp",EDGE,"E72.14"),sQuery(id+"F15.wireOp",EDGE,"E72.15")])],"isStart":true}),makeQuery(id+"F16.opExtrude","CAP_FACE",FACE,{"disambiguationData":[OSD([sQuery(id+"F15.wireOp",EDGE,"E72.9"),sQuery(id+"F15.wireOp",EDGE,"E72.10"),sQuery(id+"F15.wireOp",EDGE,"E72.11"),sQuery(id+"F15.wireOp",EDGE,"E72.12")])],"isStart":true})]});}
            var sketch = newSketch(context, id + "F17", { "sketchPlane" : qUnion([Q0])});
            skLineSegment(sketch, "E73", {"start": v(-31.5, -3.55) * mm, "end": v(-45.76, -3.55) * mm});
            skLineSegment(sketch, "E74", {"start": v(-31.5, 3.55) * mm, "end": v(-45.76, 3.55) * mm});
            skPoint(sketch, "E75.orphan", {"position": v(-46.6, -5.9) * mm});
            skLineSegment(sketch, "E76.0", {"start": v(-31.5, -3.55) * mm, "end": v(-31.5, 3.55) * mm});
            skLineSegment(sketch, "E77", {"start": v(-45.76, -3.55) * mm, "end": v(-45.76, 3.55) * mm});
            skPoint(sketch, "E78.orphan", {"position": v(-33, 3.55) * mm});
            skPoint(sketch, "E79.orphan", {"position": v(-33, -3.55) * mm});
            skSolve(sketch);
        }
        {
            var Q0;
            Q0 = qSketchRegion(id + "F17", true);
            extrude(context, id + "F18", {"entities" : qUnion([Q0]), "operationType" : NewBodyOperationType.ADD, "oppositeDirection" : true, "depth" : 3.2 * mm, "offsetDistance" : 25 * mm});
        }
        {
            var Q0;
            Q0=makeQuery(id+"F18.opExtrude","SWEPT_EDGE",EDGE,{"disambiguationData":[OSD([sQuery(id+"F17.wireOp",EDGE,"E73"),sQuery(id+"F17.wireOp",EDGE,"E76.0")])]});
            var Q1;
            Q1=makeQuery(id+"F18.opExtrude","SWEPT_EDGE",EDGE,{"disambiguationData":[OSD([sQuery(id+"F17.wireOp",EDGE,"E74"),sQuery(id+"F17.wireOp",EDGE,"E76.0")])]});
            var Q2;
            Q2=makeQuery(id+"F18.opExtrude","SWEPT_EDGE",EDGE,{"disambiguationData":[OSD([sQuery(id+"F17.wireOp",EDGE,"E73"),sQuery(id+"F17.wireOp",EDGE,"E77")])]});
            var Q3;
            Q3=makeQuery(id+"F18.opExtrude","SWEPT_EDGE",EDGE,{"disambiguationData":[OSD([sQuery(id+"F17.wireOp",EDGE,"E74"),sQuery(id+"F17.wireOp",EDGE,"E77")])]});
            var Q4;
            Q4=makeQuery(id+"F6LGgWXpaXXhIzC_1.1.F18.opExtrude","SWEPT_EDGE",EDGE,{"disambiguationData":[OSD([sQuery(id+"F17.wireOp",EDGE,"E73"),sQuery(id+"F17.wireOp",EDGE,"E76.0")])]});
            var Q5;
            Q5=makeQuery(id+"F6LGgWXpaXXhIzC_1.1.F18.opExtrude","SWEPT_EDGE",EDGE,{"disambiguationData":[OSD([sQuery(id+"F17.wireOp",EDGE,"E74"),sQuery(id+"F17.wireOp",EDGE,"E76.0")])]});
            var Q6;
            Q6=makeQuery(id+"F6LGgWXpaXXhIzC_1.1.F18.opExtrude","SWEPT_EDGE",EDGE,{"disambiguationData":[OSD([sQuery(id+"F17.wireOp",EDGE,"E73"),sQuery(id+"F17.wireOp",EDGE,"E77")])]});
            var Q7;
            Q7=makeQuery(id+"F6LGgWXpaXXhIzC_1.1.F18.opExtrude","SWEPT_EDGE",EDGE,{"disambiguationData":[OSD([sQuery(id+"F17.wireOp",EDGE,"E74"),sQuery(id+"F17.wireOp",EDGE,"E77")])]});
            fillet(context, id + "F19", {"entities" : qUnion([Q0, Q1, Q2, Q3, Q4, Q5, Q6, Q7]), "radius" : 1 * mm, "tangentPropagation" : true, "allowEdgeOverflow" : false});
        }
        {
            var Q0;
            {var subQ0=sQuery(id+"F6.wireOp",EDGE,"E48.0");var subQ1=sQuery(id+"F6.wireOp",EDGE,"E67.MirrorCS");var subQ2=sQuery(id+"F17.wireOp",EDGE,"E76.0");var subQ3=sQuery(id+"F6.wireOp",EDGE,"E54.trimOffspring");Q0=makeQuery(id+"F6LGgWXpaXXhIzC_1.1.F18.boolean.opBoolean","SPLIT",FACE,{"disambiguationData":[TD([makeQuery(id+"F18.opExtrude","SWEPT_FACE",FACE,{"disambiguationData":[OSD([subQ2])]})])],"derivedFrom":makeQuery(id+"F7.boolean.opBoolean","MERGE",FACE,{"derivedFrom":[makeQuery(id+"F5.opExtrude","CAP_FACE",FACE,{"disambiguationData":[OSD([sQuery(id+"F4.wireOp",EDGE,"E36.0"),sQuery(id+"F4.wireOp",EDGE,"E38.0")])],"isStart":false}),makeQuery(id+"F5.opExtrude","CAP_FACE",FACE,{"disambiguationData":[OSD([sQuery(id+"F4.wireOp",EDGE,"E36.1"),sQuery(id+"F4.wireOp",EDGE,"E37.0")])],"isStart":false}),makeQuery(id+"F7.opExtrude","CAP_FACE",FACE,{"disambiguationData":[OSD([sQuery(id+"F6.wireOp",EDGE,"E40.0"),sQuery(id+"F6.wireOp",EDGE,"E42.0"),sQuery(id+"F6.wireOp",EDGE,"E43.0"),subQ3])],"isStart":true}),makeQuery(id+"F7.opExtrude","CAP_FACE",FACE,{"disambiguationData":[OSD([sQuery(id+"F6.wireOp",EDGE,"E41.0"),sQuery(id+"F6.wireOp",EDGE,"E46.0"),sQuery(id+"F6.wireOp",EDGE,"E47.0"),sQuery(id+"F6.wireOp",EDGE,"E51.trimOffspring")])],"isStart":true}),makeQuery(id+"F7.opExtrude","CAP_FACE",FACE,{"disambiguationData":[OSD([sQuery(id+"F6.wireOp",EDGE,"E44.0"),sQuery(id+"F6.wireOp",EDGE,"E45.0"),sQuery(id+"F6.wireOp",EDGE,"E52.trimOffspring"),sQuery(id+"F6.wireOp",EDGE,"E53.trimOffspring")])],"isStart":true}),makeQuery(id+"F7.opExtrude","CAP_FACE",FACE,{"disambiguationData":[OSD([subQ0,sQuery(id+"F6.wireOp",EDGE,"E50.trimOffspring"),subQ3,sQuery(id+"F6.wireOp",EDGE,"E56.MirrorCS"),subQ1])],"isStart":true}),makeQuery(id+"F7.opExtrude","CAP_FACE",FACE,{"disambiguationData":[OSD([subQ3,sQuery(id+"F6.wireOp",EDGE,"E59.MirrorCS"),sQuery(id+"F6.wireOp",EDGE,"E61.MirrorCS"),sQuery(id+"F6.wireOp",EDGE,"E65.MirrorCS")])],"isStart":true}),makeQuery(id+"F7.opExtrude","CAP_FACE",FACE,{"disambiguationData":[OSD([subQ3,sQuery(id+"F6.wireOp",EDGE,"E60.MirrorCS"),sQuery(id+"F6.wireOp",EDGE,"E63.MirrorCS"),sQuery(id+"F6.wireOp",EDGE,"E66.MirrorCS")])],"isStart":true}),makeQuery(id+"F7.opExtrude","CAP_FACE",FACE,{"disambiguationData":[OSD([subQ3,sQuery(id+"F6.wireOp",EDGE,"E58.MirrorCS"),sQuery(id+"F6.wireOp",EDGE,"E62.MirrorCS"),sQuery(id+"F6.wireOp",EDGE,"E64.MirrorCS")])],"isStart":true})]})});}
            var sketch = newSketch(context, id + "F20", { "sketchPlane" : qUnion([Q0])});
            skLineSegment(sketch, "E80.0", {"start": v(-18, 4.7) * mm, "end": v(-18, 2.4) * mm});
            skLineSegment(sketch, "E81", {"start": v(0, 1.6) * mm, "end": v(0, -1.6) * mm, "construction": true});
            skLineSegment(sketch, "E82.8.0.0", {"start": v(4, 0.8) * mm, "end": v(4, -0.8) * mm});
            skLineSegment(sketch, "E82.12.0.0", {"start": v(6, 0.8) * mm, "end": v(6, 0.25) * mm});
            skLineSegment(sketch, "E82.15.0.0", {"start": v(7.5, 0.8) * mm, "end": v(7.5, 0.25) * mm});
            skLineSegment(sketch, "E82.32.0.0", {"start": v(16, 1.6) * mm, "end": v(16, 0.8) * mm});
            skLineSegment(sketch, "E82.33.0.0", {"start": v(16.5, 0.8) * mm, "end": v(16.5, -0.8) * mm});
            skLineSegment(sketch, "E82.37.0.0", {"start": v(18.5, 0.8) * mm, "end": v(18.5, -0.8) * mm});
            skLineSegment(sketch, "E82.40.0.0", {"start": v(20.29, 0.3) * mm, "end": v(20.29, -0.3) * mm});
            skLineSegment(sketch, "E83.0", {"start": v(9.5, 0.8) * mm, "end": v(9.5, 0.55) * mm});
            skLineSegment(sketch, "E84.0", {"start": v(22, 0.4) * mm, "end": v(22, -0.4) * mm});
            skLineSegment(sketch, "E85.trimOffspring", {"start": v(3.5, 1.6) * mm, "end": v(8.7, 1.6) * mm});
            skLineSegment(sketch, "E86.trimOffspring", {"start": v(3.5, 0.8) * mm, "end": v(4, 0.8) * mm});
            skLineSegment(sketch, "E87.trimOffspring", {"start": v(6, 0.25) * mm, "end": v(7.5, 0.25) * mm});
            skLineSegment(sketch, "E88.trimOffspring", {"start": v(6, -0.25) * mm, "end": v(7, -0.25) * mm});
            skLineSegment(sketch, "E89.trimOffspring", {"start": v(3.5, -0.8) * mm, "end": v(4, -0.8) * mm});
            skLineSegment(sketch, "E90.trimOffspring", {"start": v(3.5, -1.6) * mm, "end": v(6.5, -1.6) * mm});
            skPoint(sketch, "E91.MirrorCS.start.orphan", {"position": v(-31.5, -0.8) * mm});
            skLineSegment(sketch, "E92.trimOffspring", {"start": v(16, 1.6) * mm, "end": v(20.8, 1.6) * mm});
            skLineSegment(sketch, "E93.trimOffspring", {"start": v(16, -1.6) * mm, "end": v(20.8, -1.6) * mm});
            skLineSegment(sketch, "E94.trimOffspring", {"start": v(16, -0.8) * mm, "end": v(16.5, -0.8) * mm});
            skLineSegment(sketch, "E95.trimOffspring", {"start": v(16, 0.8) * mm, "end": v(16.5, 0.8) * mm});
            skLineSegment(sketch, "E96.MirrorCS", {"start": v(-16.5, 0.8) * mm, "end": v(-16.5, 0.25) * mm});
            skLineSegment(sketch, "E97.MirrorCS", {"start": v(-21.5, 0.8) * mm, "end": v(-21.5, -0.8) * mm});
            skLineSegment(sketch, "E98.MirrorCS", {"start": v(-16, 1.6) * mm, "end": v(-16, 0.25) * mm});
            skLineSegment(sketch, "E99.MirrorCS", {"start": v(-9.5, 0.4) * mm, "end": v(-9.5, -0.4) * mm});
            skLineSegment(sketch, "E100.MirrorCS", {"start": v(-6, -0.8) * mm, "end": v(-7, -0.8) * mm});
            skLineSegment(sketch, "E101.MirrorCS", {"start": v(-4.7, -1.6) * mm, "end": v(-8.3, -1.6) * mm});
            skLineSegment(sketch, "E102.MirrorCS", {"start": v(-19.5, 0.8) * mm, "end": v(-19.5, 0.25) * mm});
            skLineSegment(sketch, "E103.MirrorCS", {"start": v(-3.5, 0.4) * mm, "end": v(-3.5, -0.4) * mm});
            skLineSegment(sketch, "E104.MirrorCS", {"start": v(-6, 0.8) * mm, "end": v(-7, 0.8) * mm});
            skLineSegment(sketch, "E105.MirrorCS", {"start": v(-4.7, 1.6) * mm, "end": v(-8.3, 1.6) * mm});
            skLineSegment(sketch, "E106.MirrorCS", {"start": v(-5.5, 0.3) * mm, "end": v(-5.5, -0.3) * mm});
            skLineSegment(sketch, "E107.MirrorCS", {"start": v(-16, 1.6) * mm, "end": v(-22, 1.6) * mm});
            skLineSegment(sketch, "E108.MirrorCS", {"start": v(-16.5, 0.8) * mm, "end": v(-19.5, 0.8) * mm});
            skLineSegment(sketch, "E109.MirrorCS", {"start": v(-16, 0.25) * mm, "end": v(-16.5, 0.25) * mm});
            skLineSegment(sketch, "E110.MirrorCS", {"start": v(-17.5, 0.25) * mm, "end": v(-17.5, -0.25) * mm});
            skLineSegment(sketch, "E111.MirrorCS", {"start": v(-7.5, 0.3) * mm, "end": v(-7.5, -0.3) * mm});
            skLineSegment(sketch, "E112.trimOffspring", {"start": v(-22, -0.8) * mm, "end": v(-22, -1.6) * mm});
            skLineSegment(sketch, "E113", {"start": v(-22, 1.6) * mm, "end": v(-22, 0.8) * mm});
            skLineSegment(sketch, "E114.trimOffspring", {"start": v(-21.5, 0.8) * mm, "end": v(-22, 0.8) * mm});
            skLineSegment(sketch, "E115.trimOffspring", {"start": v(-21.5, -0.8) * mm, "end": v(-22, -0.8) * mm});
            skLineSegment(sketch, "E116.trimOffspring", {"start": v(-19, -1.6) * mm, "end": v(-22, -1.6) * mm});
            skLineSegment(sketch, "E117.trimOffspring", {"start": v(-19, -0.8) * mm, "end": v(-19.5, -0.8) * mm});
            skLineSegment(sketch, "E118.trimOffspring", {"start": v(-19.5, -0.25) * mm, "end": v(-19.5, -0.8) * mm});
            skLineSegment(sketch, "E119.trimOffspring", {"start": v(-17.5, 0.25) * mm, "end": v(-19.5, 0.25) * mm});
            skLineSegment(sketch, "E120.trimOffspring", {"start": v(-17.5, -0.25) * mm, "end": v(-19.5, -0.25) * mm});
            skLineSegment(sketch, "E121.trimOffspring", {"start": v(-19, -0.8) * mm, "end": v(-19, -1.6) * mm});
            skLineSegment(sketch, "E122.trimOffspring", {"start": v(3.5, -0.8) * mm, "end": v(3.5, -1.6) * mm});
            skLineSegment(sketch, "E123", {"start": v(3.5, 1.6) * mm, "end": v(3.5, 0.8) * mm});
            skLineSegment(sketch, "E124.trimOffspring", {"start": v(6, 0.8) * mm, "end": v(7.5, 0.8) * mm});
            skPoint(sketch, "E125.orphan", {"position": v(5.5, -1.6) * mm});
            skPoint(sketch, "E126.orphan", {"position": v(7.5, -1.6) * mm});
            skLineSegment(sketch, "E127.trimOffspring", {"start": v(7.5, -1.6) * mm, "end": v(9.5, -1.6) * mm});
            skLineSegment(sketch, "E128", {"start": v(7.5, -1.6) * mm, "end": v(7, -0.25) * mm});
            skLineSegment(sketch, "E129", {"start": v(9, -0.8) * mm, "end": v(8.74, -0.25) * mm});
            skPoint(sketch, "E130.orphan", {"position": v(5.5, 1.6) * mm});
            skPoint(sketch, "E131.orphan", {"position": v(7.5, 1.6) * mm});
            skPoint(sketch, "E132.orphan", {"position": v(9.5, 0.8) * mm});
            skLineSegment(sketch, "E133.trimOffspring", {"start": v(9.5, -0.8) * mm, "end": v(9.5, -1.6) * mm});
            skLineSegment(sketch, "E134", {"start": v(6.5, -0.8) * mm, "end": v(6, -0.8) * mm});
            skLineSegment(sketch, "E135.trimOffspring", {"start": v(6.5, -0.8) * mm, "end": v(6.5, -1.6) * mm});
            skLineSegment(sketch, "E136.trimOffspring", {"start": v(6, -0.25) * mm, "end": v(6, -0.8) * mm});
            skLineSegment(sketch, "E137.trimOffspring", {"start": v(9, -0.8) * mm, "end": v(9.5, -0.8) * mm});
            skLineSegment(sketch, "E138.trimOffspring", {"start": v(8.7, -0.25) * mm, "end": v(8.74, -0.25) * mm});
            skPoint(sketch, "E139.orphan", {"position": v(-3.5, 0.8) * mm});
            skPoint(sketch, "E140.orphan", {"position": v(-5.5, 1.6) * mm});
            skPoint(sketch, "E141.orphan", {"position": v(-7.5, 1.6) * mm});
            skPoint(sketch, "E142.orphan", {"position": v(-9.5, 0.8) * mm});
            skPoint(sketch, "E143.orphan", {"position": v(-9.5, -0.8) * mm});
            skPoint(sketch, "E144.orphan", {"position": v(-5.5, -1.6) * mm});
            skPoint(sketch, "E145.orphan", {"position": v(-3.5, -0.8) * mm});
            skPoint(sketch, "E146.orphan", {"position": v(-7.5, -1.6) * mm});
            skLineSegment(sketch, "E147.trimOffspring", {"start": v(16, -0.8) * mm, "end": v(16, -1.6) * mm});
            skPoint(sketch, "E148.orphan", {"position": v(22, 0.8) * mm});
            skPoint(sketch, "E149.orphan", {"position": v(22, -0.8) * mm});
            skLineSegment(sketch, "E150.trimOffspring", {"start": v(18.5, -0.8) * mm, "end": v(19.79, -0.8) * mm});
            skLineSegment(sketch, "E151.trimOffspring", {"start": v(18.5, 0.8) * mm, "end": v(19.79, 0.8) * mm});
            skPoint(sketch, "E152.visualSharp", {"position": v(-9.5, 1.6) * mm});
            skArc(sketch, "E152.filletArc", {"start": v(-8.3, 1.6) * mm, "mid": v(-9.15, 1.25) * mm, "end": v(-9.5, 0.4) * mm});
            skPoint(sketch, "E153.visualSharp", {"position": v(-3.5, 1.6) * mm});
            skArc(sketch, "E153.filletArc", {"start": v(-3.5, 0.4) * mm, "mid": v(-3.85, 1.25) * mm, "end": v(-4.7, 1.6) * mm});
            skPoint(sketch, "E154.visualSharp", {"position": v(-3.5, -1.6) * mm});
            skArc(sketch, "E154.filletArc", {"start": v(-4.7, -1.6) * mm, "mid": v(-3.85, -1.25) * mm, "end": v(-3.5, -0.4) * mm});
            skPoint(sketch, "E155.visualSharp", {"position": v(-9.5, -1.6) * mm});
            skArc(sketch, "E155.filletArc", {"start": v(-9.5, -0.4) * mm, "mid": v(-9.15, -1.25) * mm, "end": v(-8.3, -1.6) * mm});
            skPoint(sketch, "E156.visualSharp", {"position": v(22, 1.6) * mm});
            skArc(sketch, "E156.filletArc", {"start": v(22, 0.4) * mm, "mid": v(21.65, 1.25) * mm, "end": v(20.8, 1.6) * mm});
            skPoint(sketch, "E157.visualSharp", {"position": v(22, -1.6) * mm});
            skArc(sketch, "E157.filletArc", {"start": v(20.8, -1.6) * mm, "mid": v(21.65, -1.25) * mm, "end": v(22, -0.4) * mm});
            skPoint(sketch, "E158.visualSharp", {"position": v(9.5, 1.6) * mm});
            skArc(sketch, "E158.filletArc", {"start": v(9.5, 0.8) * mm, "mid": v(9.27, 1.37) * mm, "end": v(8.7, 1.6) * mm});
            skPoint(sketch, "E159.visualSharp", {"position": v(9.5, -0.25) * mm});
            skArc(sketch, "E159.filletArc", {"start": v(8.7, -0.25) * mm, "mid": v(9.27, -0.02) * mm, "end": v(9.5, 0.55) * mm});
            skPoint(sketch, "E160.visualSharp", {"position": v(20.29, -0.8) * mm});
            skArc(sketch, "E160.filletArc", {"start": v(19.79, -0.8) * mm, "mid": v(20.14, -0.65) * mm, "end": v(20.29, -0.3) * mm});
            skPoint(sketch, "E161.visualSharp", {"position": v(20.29, 0.8) * mm});
            skArc(sketch, "E161.filletArc", {"start": v(20.29, 0.3) * mm, "mid": v(20.14, 0.65) * mm, "end": v(19.79, 0.8) * mm});
            skPoint(sketch, "E162.visualSharp", {"position": v(-5.5, 0.8) * mm});
            skPoint(sketch, "E163.visualSharp", {"position": v(-5.5, -0.8) * mm});
            skArc(sketch, "E163.filletArc", {"start": v(-6, -0.8) * mm, "mid": v(-5.65, -0.65) * mm, "end": v(-5.5, -0.3) * mm});
            skPoint(sketch, "E164.visualSharp", {"position": v(-7.5, -0.8) * mm});
            skArc(sketch, "E164.filletArc", {"start": v(-7.5, -0.3) * mm, "mid": v(-7.35, -0.65) * mm, "end": v(-7, -0.8) * mm});
            skPoint(sketch, "E165.visualSharp", {"position": v(-7.5, 0.8) * mm});
            skArc(sketch, "E165.filletArc", {"start": v(-7, 0.8) * mm, "mid": v(-7.35, 0.65) * mm, "end": v(-7.5, 0.3) * mm});
            skArc(sketch, "E166.filletArc", {"start": v(-5.5, 0.3) * mm, "mid": v(-5.65, 0.65) * mm, "end": v(-6, 0.8) * mm});
            skSolve(sketch);
        }
        {
            var Q0;
            Q0 = qSketchRegion(id + "F20", true);
            extrude(context, id + "F21", {"entities" : qUnion([Q0]), "operationType" : NewBodyOperationType.ADD, "depth" : 1 * mm, "offsetDistance" : 25 * mm});
        }
        {
            var Q0;
            Q0=makeQuery(id+"F18.opExtrude","CAP_FACE",FACE,{"disambiguationData":[OSD([sQuery(id+"F17.wireOp",EDGE,"E73"),sQuery(id+"F17.wireOp",EDGE,"E74"),sQuery(id+"F17.wireOp",EDGE,"E76.0"),sQuery(id+"F17.wireOp",EDGE,"E77")])],"isStart":false});
            var sketch = newSketch(context, id + "F22", { "sketchPlane" : qUnion([Q0])});
            skArc(sketch, "E167.0", {"start": v(-32.5, -3.05) * mm, "mid": v(-32.15, -2.9) * mm, "end": v(-32, -2.55) * mm});
            skLineSegment(sketch, "E167.1", {"start": v(-44.76, -3.05) * mm, "end": v(-32.5, -3.05) * mm});
            skLineSegment(sketch, "E167.2", {"start": v(-32, -2.55) * mm, "end": v(-32, 2.55) * mm});
            skArc(sketch, "E167.3", {"start": v(-45.26, -2.55) * mm, "mid": v(-45.1, -2.9) * mm, "end": v(-44.76, -3.05) * mm});
            skArc(sketch, "E167.4", {"start": v(-32, 2.55) * mm, "mid": v(-32.15, 2.9) * mm, "end": v(-32.5, 3.05) * mm});
            skLineSegment(sketch, "E167.5", {"start": v(-32.5, 3.05) * mm, "end": v(-44.76, 3.05) * mm});
            skArc(sketch, "E167.6", {"start": v(-44.76, 3.05) * mm, "mid": v(-45.1, 2.9) * mm, "end": v(-45.26, 2.55) * mm});
            skLineSegment(sketch, "E167.7", {"start": v(-45.26, 2.55) * mm, "end": v(-45.26, -2.55) * mm});
            skArc(sketch, "E168.0", {"start": v(45.26, 2.55) * mm, "mid": v(45.1, 2.9) * mm, "end": v(44.76, 3.05) * mm});
            skLineSegment(sketch, "E168.1", {"start": v(45.26, -2.55) * mm, "end": v(45.26, 2.55) * mm});
            skLineSegment(sketch, "E168.2", {"start": v(44.76, 3.05) * mm, "end": v(32.5, 3.05) * mm});
            skArc(sketch, "E168.3", {"start": v(44.76, -3.05) * mm, "mid": v(45.1, -2.9) * mm, "end": v(45.26, -2.55) * mm});
            skArc(sketch, "E168.4", {"start": v(32.5, 3.05) * mm, "mid": v(32.15, 2.9) * mm, "end": v(32, 2.55) * mm});
            skLineSegment(sketch, "E168.5", {"start": v(32, 2.55) * mm, "end": v(32, -2.55) * mm});
            skArc(sketch, "E168.6", {"start": v(32, -2.55) * mm, "mid": v(32.15, -2.9) * mm, "end": v(32.5, -3.05) * mm});
            skLineSegment(sketch, "E168.7", {"start": v(32.5, -3.05) * mm, "end": v(44.76, -3.05) * mm});
            skSolve(sketch);
        }
        {
            var Q0;
            Q0 = qSketchRegion(id + "F22", true);
            extrude(context, id + "F23", {"entities" : qUnion([Q0]), "operationType" : NewBodyOperationType.REMOVE, "oppositeDirection" : true, "depth" : 25 * mm, "offsetDistance" : 25 * mm});
        }
        {
            var Q0;
            Q0=makeQuery(id+"F9.opExtrude","CAP_FACE",FACE,{"disambiguationData":[OSD([sQuery(id+"F8.wireOp",EDGE,"E69.0"),sQuery(id+"F8.wireOp",EDGE,"E70.0")])],"isStart":false});
            var sketch = newSketch(context, id + "F24", { "sketchPlane" : qUnion([Q0])});
            skCircle(sketch, "E169", {"center": v(-46.8, 0) * mm, "radius": 1.5 * mm});
            skPoint(sketch, "E170", {"position": v(-59.35, 0) * mm});
            skCircle(sketch, "E171.1.0", {"center": v(-65.62, 10.87) * mm, "radius": 1.5 * mm});
            skCircle(sketch, "E171.2.0", {"center": v(-65.62, -10.87) * mm, "radius": 1.5 * mm});
            skCircle(sketch, "E172.MirrorC", {"center": v(46.8, 0) * mm, "radius": 1.5 * mm});
            skCircle(sketch, "E173.MirrorC", {"center": v(65.62, 10.87) * mm, "radius": 1.5 * mm});
            skCircle(sketch, "E174.MirrorC", {"center": v(65.62, -10.87) * mm, "radius": 1.5 * mm});
            skSolve(sketch);
        }
        {
            var Q0;
            Q0 = qSketchRegion(id + "F24", true);
            extrude(context, id + "F25", {"entities" : qUnion([Q0]), "operationType" : NewBodyOperationType.REMOVE, "oppositeDirection" : true, "depth" : 1.5 * mm, "offsetDistance" : 25 * mm});
        }
    });
